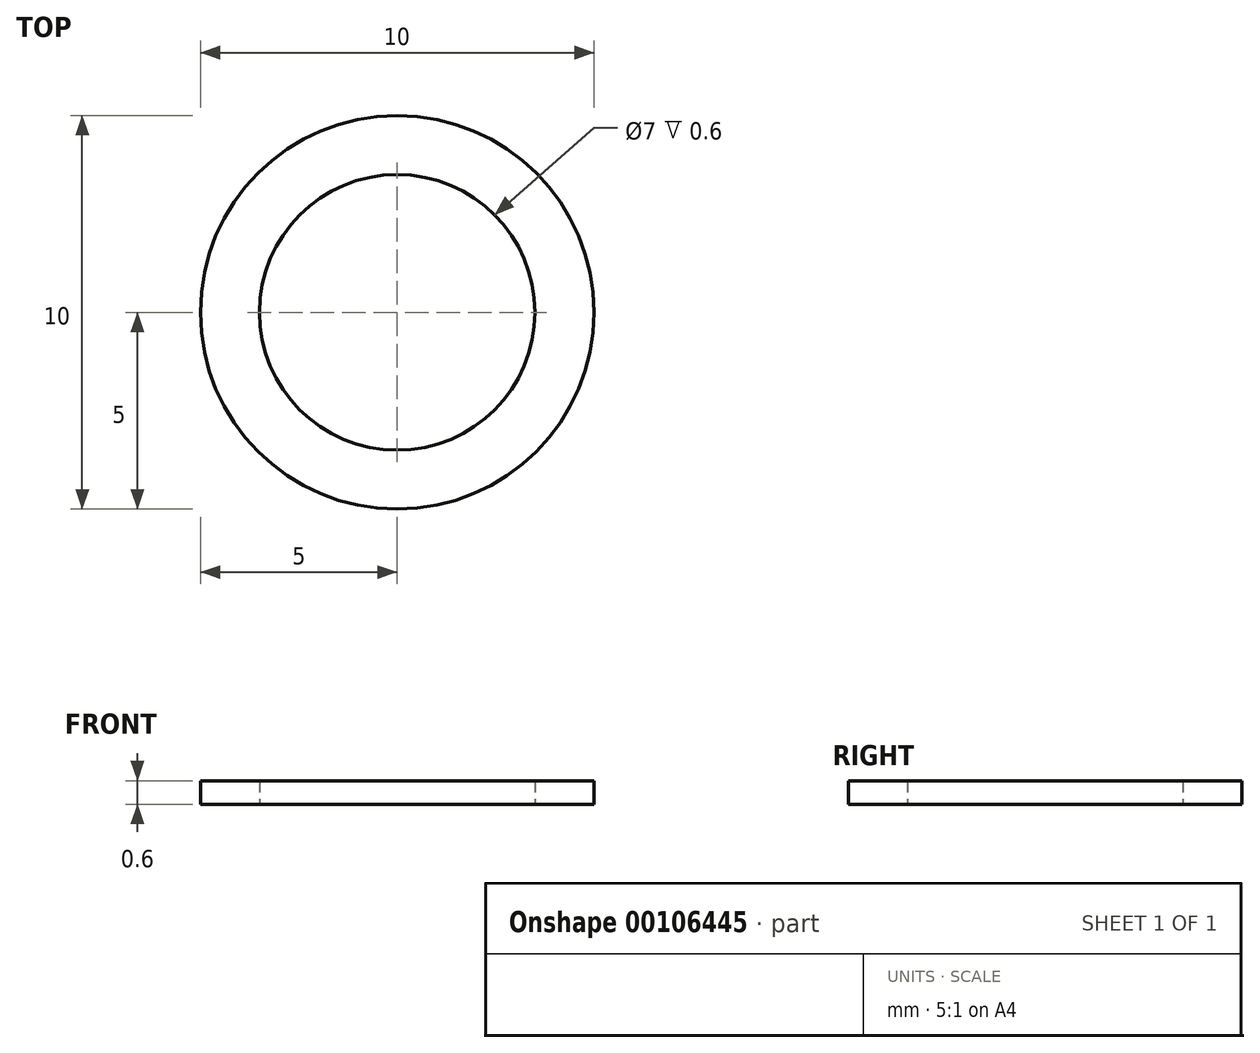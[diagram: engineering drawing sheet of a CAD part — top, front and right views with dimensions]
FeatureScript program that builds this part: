
annotation { "Feature Type Name" : "Feature", "Feature Type Description" : "" }
export const myFeature = defineFeature(function(context is Context, id is Id, definition is map)
    precondition{}
    {
        {
            var Q0;
            Q0=qCreatedBy(makeId("Top.planeOp"),FACE);
            var sketch = newSketch(context, id + "F0", { "sketchPlane" : qUnion([Q0])});
            skCircle(sketch, "E0", {"center": v(0, 0) * mm, "radius": 5 * mm});
            skCircle(sketch, "E1", {"center": v(0, 0) * mm, "radius": 3.5 * mm});
            skSolve(sketch);
        }
        {
            var Q0;
            Q0=makeQuery(id+"F0.imprint","IMPRINT",FACE,{"disambiguationData":[TD([[makeQuery(id+"F0.imprint","IMPRINT",EDGE,{"derivedFrom":sQuery(id+"F0.wireOp",EDGE,"E0")}),1.0]])]});
            extrude(context, id + "F1", {"entities" : qUnion([Q0]), "depth" : 0.6 * mm});
        }
    });
